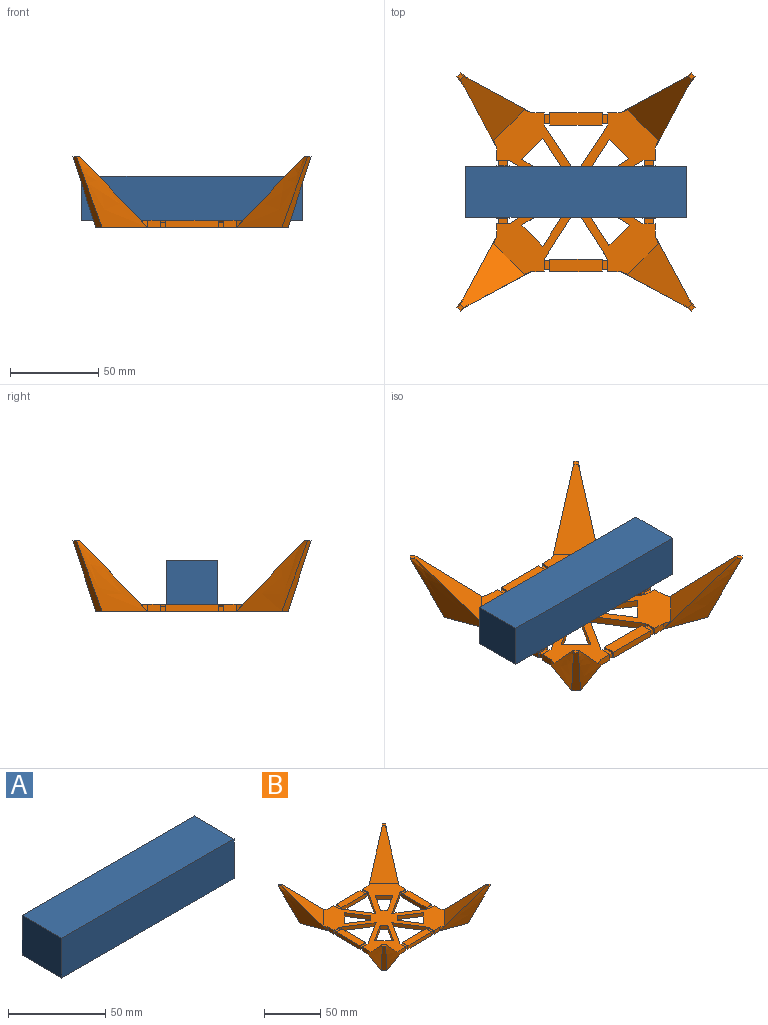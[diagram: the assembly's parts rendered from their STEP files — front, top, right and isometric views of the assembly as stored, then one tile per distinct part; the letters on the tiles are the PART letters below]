
ASSEMBLY  parts=2 mates=1
PART A: 11 faces, bbox 125.1x29x25 mm
  f0: plane 28.98x25mm, normal (1,0,0), area 199.9mm2, adj f1,f3,f4,f5,f6,f8,f9,f10
  f1: plane 125.11x25mm, normal (0,1,0), area 3127.8mm2, adj f0,f2,f4,f5
  f2: plane 28.98x25mm, normal (-1,0,0), area 724.4mm2, adj f1,f3,f4,f5
  f3: plane 125.11x25mm, normal (0,-1,0), area 3127.8mm2, adj f0,f2,f4,f5
  f4: plane 125.11x28.98mm, normal (0,0,1), area 3625.5mm2, adj f0,f1,f2,f3
  f5: plane 125.11x28.98mm, normal (0,0,-1), area 3625.5mm2, adj f0,f1,f2,f3
  f6: plane 123.11x21mm, normal (0,-1,0), area 2585.4mm2, adj f0,f7,f9,f10
  f7: plane 24.98x21mm, normal (1,0,0), area 524.5mm2, adj f6,f8,f9,f10
  f8: plane 123.11x21mm, normal (0,1,0), area 2585.4mm2, adj f0,f7,f9,f10
  f9: plane 123.11x24.98mm, normal (0,0,-1), area 3075mm2, adj f0,f6,f7,f8
  f10: plane 123.11x24.98mm, normal (0,0,1), area 3075mm2, adj f0,f6,f7,f8
PART B: 169 faces, bbox 135x135x40 mm
  f0: plane 108.95x108.91mm, normal (0,0,-1), area 4796.5mm2, adj f1,f2,f3,f4,f5,f6,f7,f8
  f1: plane 3x3mm, normal (0,-1,0), area 9mm2, adj f0,f19,f20,f111
  f2: plane 3x2.99mm, normal (0,1,0), area 9mm2, adj f0,f40,f41,f107
  f3: plane 3x3mm, normal (-1,0,0), area 9mm2, adj f0,f50,f51,f109
  f4: plane 3x2.98mm, normal (-1,0,0), area 8.9mm2, adj f0,f53,f97,f110
  f5: plane 3x3mm, normal (0,1,0), area 9mm2, adj f0,f57,f58,f112
  f6: plane 3x2.99mm, normal (0.01,-1,0), area 9mm2, adj f0,f71,f72,f101
  f7: plane 4x3mm, normal (0,-1,0), area 9mm2, adj f0,f41,f74,f75,f98,f107
  f8: plane 3x3mm, normal (1,0,0), area 9mm2, adj f0,f50,f86,f109
  f9: plane 3x2.98mm, normal (1,0,0), area 8.9mm2, adj f0,f89,f97,f110
  f10: plane 3x3mm, normal (0,1,0), area 9mm2, adj f0,f20,f54,f111
  f11: plane 29.88x7.06mm, normal (0,0,1), area 210.8mm2, adj f31,f32,f33,f64,f65,f66,f104
  f12: plane 93.17x93.16mm, normal (0,0,1), area 3663.2mm2, adj f15,f16,f17,f18,f19,f24,f25,f26
  f13: plane 29.88x7.07mm, normal (0,0,1), area 211.3mm2, adj f51,f52,f53,f86,f89,f96,f108
  f14: plane 29.86x7.06mm, normal (0,0,1), area 210.5mm2, adj f20,f21,f22,f23,f58,f59
  f15: plane 7.08x4mm, normal (-1,0,0), area 28.3mm2, adj f0,f12,f16,f97
  f16: plane 4.36x4.03mm, normal (-0.94,0.34,0), area 9.2mm2, adj f12,f15,f120
  f17: plane 4.35x4.03mm, normal (0.34,-0.94,0), area 9.2mm2, adj f12,f18,f120
  f18: plane 7.08x4mm, normal (0,-1,0), area 28.3mm2, adj f0,f12,f17,f19
  f19: plane 4x1mm, normal (1,0,0), area 4mm2, adj f0,f1,f12,f18,f54
  f20: plane 7.04x4mm, normal (-1,0,0), area 12.9mm2, adj f0,f1,f10,f14,f21,f59,f111
  f21: plane 29.85x4mm, normal (0,-1,0), area 119.4mm2, adj f0,f14,f20,f22
  f22: plane 4x0.99mm, normal (1,0,0), area 3.9mm2, adj f0,f14,f21,f23
  f23: plane 4x3.02mm, normal (0,-1,0), area 9.1mm2, adj f0,f14,f22,f24,f58,f112
  f24: plane 6.07x4mm, normal (-1,0,0), area 9mm2, adj f0,f12,f23,f25,f57,f112
  f25: plane 7.07x4mm, normal (0,-1,0), area 28.3mm2, adj f0,f12,f24,f26
  f26: plane 4.36x4.03mm, normal (-0.34,-0.94,0), area 9.2mm2, adj f12,f25,f116
  f27: plane 4.35x4.03mm, normal (0.94,0.34,0), area 9.2mm2, adj f12,f28,f116
  f28: plane 7.08x4mm, normal (1,0,0), area 28.3mm2, adj f0,f12,f27,f29
  f29: plane 4x1mm, normal (0,1,0), area 4mm2, adj f0,f12,f28,f30,f102
  f30: plane 3x2.98mm, normal (1,0,0), area 8.9mm2, adj f0,f29,f31,f103
  f31: plane 6.08x4.01mm, normal (0,-1,0), area 9mm2, adj f0,f11,f30,f32,f66,f103
  f32: plane 29.87x4mm, normal (1,0,0), area 119.5mm2, adj f0,f11,f31,f33
  f33: plane 4.01x1mm, normal (0,1,0), area 4mm2, adj f0,f11,f32,f34,f104
  f34: plane 3x3mm, normal (1,0,0), area 9mm2, adj f0,f33,f35,f105
  f35: plane 6.1x4mm, normal (0,-1,0), area 9.1mm2, adj f0,f12,f34,f36,f62,f105
  f36: plane 7.07x4mm, normal (1,0,0), area 28.3mm2, adj f0,f12,f35,f37
  f37: plane 4.36x4.03mm, normal (0.94,-0.34,0), area 9.2mm2, adj f12,f36,f126
  f38: plane 4.35x4.03mm, normal (-0.34,0.94,0), area 9.2mm2, adj f12,f39,f126
  f39: plane 7.08x4mm, normal (0,1,0), area 28.3mm2, adj f0,f12,f38,f40
  f40: plane 4.01x1.01mm, normal (-1,0,0), area 4mm2, adj f0,f2,f12,f39,f106
  f41: plane 6.09x4mm, normal (1,0,0), area 9.1mm2, adj f0,f2,f7,f42,f98,f107
  f42: plane 29.87x4mm, normal (0,1,0), area 119.5mm2, adj f0,f41,f43,f98
  f43: plane 6.08x4mm, normal (-1,0,0), area 9mm2, adj f0,f42,f44,f98,f100,f101
  f44: plane 3x2.99mm, normal (0,1,0), area 9mm2, adj f0,f43,f45,f101
  f45: plane 4.01x0.96mm, normal (1,0,0), area 3.8mm2, adj f0,f12,f44,f46,f99
  f46: plane 7.08x4mm, normal (0,1,0), area 28.3mm2, adj f0,f12,f45,f47
  f47: plane 4.35x4.03mm, normal (0.34,0.94,0), area 9.2mm2, adj f12,f46,f131
  f48: plane 4.35x4.03mm, normal (-0.94,-0.34,0), area 9.2mm2, adj f12,f49,f131
  f49: plane 7.09x4mm, normal (-1,0,0), area 28.4mm2, adj f0,f12,f48,f50
  f50: plane 7.09x4mm, normal (0,-1,0), area 13.1mm2, adj f0,f3,f8,f12,f49,f87,f109
  f51: plane 4x1mm, normal (0,1,0), area 4mm2, adj f0,f3,f13,f52,f108
  f52: plane 29.87x4mm, normal (-1,0,0), area 119.5mm2, adj f0,f13,f51,f53
  f53: plane 6.09x4.01mm, normal (0,-1,0), area 9.1mm2, adj f0,f4,f13,f52,f89,f110
  f54: plane 6.07x4mm, normal (1,0,0), area 9mm2, adj f0,f10,f12,f19,f55,f111
  f55: plane 27.99x17.94mm, normal (0.84,-0.54,0), area 133mm2, adj f0,f12,f54,f56
  f56: plane 27.98x17.92mm, normal (-0.84,-0.54,0), area 132.9mm2, adj f0,f12,f55,f57
  f57: plane 4x1.01mm, normal (-1,0,0), area 4mm2, adj f0,f5,f12,f24,f56
  f58: plane 6.07x4mm, normal (1,0,0), area 9.1mm2, adj f0,f5,f14,f23,f59,f112
  f59: plane 29.86x4mm, normal (0,1,0), area 119.4mm2, adj f0,f14,f20,f58
  f60: plane 27.99x17.91mm, normal (0.54,0.84,0), area 132.9mm2, adj f0,f12,f61,f90
  f61: plane 27.99x17.94mm, normal (0.54,-0.84,0), area 133mm2, adj f0,f12,f60,f62
  f62: plane 4x0.96mm, normal (0,-1,0), area 3.9mm2, adj f0,f12,f35,f61,f63
  f63: plane 3x3mm, normal (-1,0,0), area 9mm2, adj f0,f62,f64,f105
  f64: plane 4x0.96mm, normal (0,1,0), area 3.9mm2, adj f0,f11,f63,f65,f104
  f65: plane 29.87x4mm, normal (-1,0,0), area 119.5mm2, adj f0,f11,f64,f66
  f66: plane 4.01x1mm, normal (0,-1,0), area 3.9mm2, adj f0,f11,f31,f65,f67
  f67: plane 3x2.98mm, normal (-1,0,0), area 8.9mm2, adj f0,f66,f90,f103
  f68: plane 19.97x12.79mm, normal (0.84,0.54,0), area 94.9mm2, adj f0,f12,f69,f91
  f69: plane 4.78x4.7mm, normal (0.71,-0.7,0), area 26.8mm2, adj f0,f12,f68,f70
  f70: plane 19.84x12.97mm, normal (-0.55,-0.84,0), area 94.8mm2, adj f0,f12,f69,f91
  f71: plane 4x0.99mm, normal (1,0,0), area 3.9mm2, adj f0,f6,f12,f92,f99
  f72: plane 4x1.01mm, normal (-1,0,0), area 4mm2, adj f0,f6,f73,f98,f100,f101
  f73: plane 29.86x4mm, normal (0,-1,0), area 119.4mm2, adj f0,f72,f74,f98
  f74: plane 4x0.99mm, normal (1,0,0), area 3.9mm2, adj f0,f7,f73,f98
  f75: plane 4x0.99mm, normal (-1,0,0), area 3.9mm2, adj f0,f7,f12,f76,f106
  f76: plane 27.72x17.92mm, normal (-0.84,0.54,0), area 132mm2, adj f0,f12,f75,f92
  f77: plane 11.94x11.84mm, normal (0.71,-0.7,0), area 67.3mm2, adj f0,f12,f78,f93
  f78: plane 20.16x12.91mm, normal (-0.84,-0.54,0), area 95.8mm2, adj f0,f12,f77,f79
  f79: plane 4.65x4.64mm, normal (-0.71,0.71,0), area 26.3mm2, adj f0,f12,f78,f93
  f80: plane 19.32x12.5mm, normal (-0.54,0.84,0), area 92mm2, adj f0,f12,f81,f94
  f81: plane 4.23x4.22mm, normal (0.71,0.71,0), area 23.9mm2, adj f0,f12,f80,f82
  f82: plane 19.4x12.41mm, normal (0.84,-0.54,0), area 92.1mm2, adj f0,f12,f81,f94
  f83: plane 11.88x11.86mm, normal (0.71,0.71,0), area 67.2mm2, adj f0,f12,f84,f95
  f84: plane 20.08x12.86mm, normal (0.54,-0.84,0), area 95.4mm2, adj f0,f12,f83,f85
  f85: plane 4.67x4.66mm, normal (-0.71,-0.71,0), area 26.4mm2, adj f0,f12,f84,f95
  f86: plane 4x1mm, normal (0,1,0), area 4mm2, adj f0,f8,f13,f96,f108
  f87: plane 27.97x17.94mm, normal (-0.54,-0.84,0), area 132.9mm2, adj f0,f12,f50,f88
  f88: plane 27.97x17.91mm, normal (-0.54,0.84,0), area 132.9mm2, adj f0,f12,f87,f97
  f89: plane 4.01x1mm, normal (0,-1,0), area 4mm2, adj f0,f9,f13,f53,f96
  f90: plane 4x0.99mm, normal (0,1,0), area 3.9mm2, adj f0,f12,f60,f67,f102
  f91: plane 11.78x11.76mm, normal (-0.71,0.71,0), area 66.6mm2, adj f0,f12,f68,f70
  f92: plane 27.73x17.94mm, normal (0.84,0.54,0), area 132.1mm2, adj f0,f12,f71,f76
  f93: plane 20.11x12.86mm, normal (0.54,0.84,0), area 95.5mm2, adj f0,f12,f77,f79
  f94: plane 11.14x11.12mm, normal (-0.71,-0.71,0), area 63mm2, adj f0,f12,f80,f82
  f95: plane 20.06x12.86mm, normal (-0.84,0.54,0), area 95.3mm2, adj f0,f12,f83,f85
  f96: plane 29.87x4mm, normal (1,0,0), area 119.5mm2, adj f0,f13,f86,f89
  f97: plane 7.09x4mm, normal (0,1,0), area 13.1mm2, adj f0,f4,f9,f12,f15,f88,f110
  f98: plane 29.87x7.08mm, normal (0,0,1), area 211.3mm2, adj f7,f41,f42,f43,f72,f73,f74,f100
  f99: plane 5.11x1.01mm, normal (1,0,0), area 5.1mm2, adj f12,f45,f71,f101
  f100: plane 1x0mm, normal (0,1,0), area 0mm2, adj f43,f72,f98,f101
  f101: plane 5.1x3mm, normal (0,0,1), area 15.3mm2, adj f6,f43,f44,f72,f99,f100
  f102: plane 5.08x1mm, normal (0,1,0), area 5.1mm2, adj f12,f29,f90,f103
  f103: plane 5.08x2.98mm, normal (0,0,1), area 15.1mm2, adj f30,f31,f67,f102
  f104: plane 5.11x1.01mm, normal (0,1,0), area 5.1mm2, adj f11,f33,f64,f105
  f105: plane 5.1x3mm, normal (0,0,1), area 15.3mm2, adj f34,f35,f63,f104
  f106: plane 5.12x1.01mm, normal (-1,0,0), area 5.1mm2, adj f12,f40,f75,f107
  f107: plane 5.11x2.99mm, normal (0,0,1), area 15.3mm2, adj f2,f7,f41,f106
  f108: plane 5.08x1mm, normal (0,1,0), area 5.1mm2, adj f13,f51,f86,f109
  f109: plane 5.07x3mm, normal (0,0,1), area 15.2mm2, adj f3,f8,f50,f108
  f110: plane 5.09x2.98mm, normal (0,0,1), area 15.2mm2, adj f4,f9,f53,f97
  f111: plane 5.09x3mm, normal (0,0,1), area 15.3mm2, adj f1,f10,f20,f54
  f112: plane 5.07x3mm, normal (0,0,1), area 15.2mm2, adj f5,f23,f24,f58
  f113: plane 4x4mm, normal (0,0,1), area 8mm2, adj f114,f115,f116,f117
  f114: bspline ~40x16.66mm, area 175.4mm2, adj f0,f113,f115,f117
  f115: bspline ~40.51x40mm, area 610.2mm2, adj f0,f113,f114,f116
  f116: bspline ~40.51x40.51mm, area 747.1mm2, adj f12,f26,f27,f113,f115,f117
  f117: bspline ~40.51x40mm, area 609.5mm2, adj f0,f113,f114,f116
  f118: plane 4x4mm, normal (0,0,1), area 8mm2, adj f119,f120,f121,f122
  f119: bspline ~40.51x40mm, area 610.9mm2, adj f0,f118,f120,f122
  f120: bspline ~40.51x40.49mm, area 747.1mm2, adj f12,f16,f17,f118,f119,f121
  f121: bspline ~40.49x40mm, area 610.2mm2, adj f0,f118,f120,f122
  f122: bspline ~40x16.6mm, area 174.8mm2, adj f0,f118,f119,f121
  f123: plane 4x4mm, normal (0,0,1), area 8mm2, adj f124,f125,f126,f127
  f124: bspline ~40x16.63mm, area 175.2mm2, adj f0,f123,f125,f127
  f125: bspline ~40.49x40mm, area 610.4mm2, adj f0,f123,f124,f126
  f126: bspline ~40.51x40.49mm, area 747.1mm2, adj f12,f37,f38,f123,f125,f127
  f127: bspline ~40.51x40mm, area 610mm2, adj f0,f123,f124,f126
  f128: plane 4x4mm, normal (0,0,1), area 8mm2, adj f129,f130,f131,f132
  f129: bspline ~40x16.62mm, area 174.8mm2, adj f0,f128,f130,f132
  f130: bspline ~40.49x40mm, area 609.7mm2, adj f0,f128,f129,f131
  f131: bspline ~40.49x40.47mm, area 746.2mm2, adj f12,f47,f48,f128,f130,f132
  f132: bspline ~40.47x40mm, area 609.5mm2, adj f0,f128,f129,f131
  f133: plane 17.94x17.94mm, normal (-0.71,0.71,0), area 12.7mm2, adj f134,f136,f137,f162
  f134: plane 3.54x3.54mm, normal (-0.71,-0.71,0), area 2.5mm2, adj f133,f135,f137,f164
  f135: plane 17.94x17.94mm, normal (0.71,-0.71,0), area 12.7mm2, adj f134,f136,f137,f163
  f136: plane 3.54x3.54mm, normal (0.71,0.71,0), area 2.5mm2, adj f133,f135,f137,f161
  f137: plane 21.48x21.48mm, normal (0,0,-1), area 126.9mm2, adj f133,f134,f135,f136
  f138: plane 17.94x17.94mm, normal (0.71,-0.71,0), area 12.7mm2, adj f139,f141,f142,f154
  f139: plane 3.54x3.54mm, normal (0.71,0.71,0), area 2.5mm2, adj f138,f140,f142,f156
  f140: plane 17.94x17.94mm, normal (-0.71,0.71,0), area 12.7mm2, adj f139,f141,f142,f155
  f141: plane 3.54x3.54mm, normal (-0.71,-0.71,0), area 2.5mm2, adj f138,f140,f142,f153
  f142: plane 21.48x21.48mm, normal (0,0,-1), area 126.9mm2, adj f138,f139,f140,f141
  f143: plane 17.94x17.94mm, normal (-0.71,-0.71,0), area 12.7mm2, adj f144,f146,f147,f166
  f144: plane 3.54x3.54mm, normal (0.71,-0.71,0), area 2.5mm2, adj f143,f145,f147,f168
  f145: plane 17.94x17.94mm, normal (0.71,0.71,0), area 12.7mm2, adj f144,f146,f147,f167
  f146: plane 3.54x3.54mm, normal (-0.71,0.71,0), area 2.5mm2, adj f143,f145,f147,f165
  f147: plane 21.48x21.48mm, normal (0,0,-1), area 126.9mm2, adj f143,f144,f145,f146
  f148: plane 17.94x17.94mm, normal (0.71,0.71,0), area 12.7mm2, adj f149,f151,f152,f158
  f149: plane 3.54x3.54mm, normal (-0.71,0.71,0), area 2.5mm2, adj f148,f150,f152,f157
  f150: plane 17.94x17.94mm, normal (-0.71,-0.71,0), area 12.7mm2, adj f149,f151,f152,f159
  f151: plane 3.54x3.54mm, normal (0.71,-0.71,0), area 2.5mm2, adj f148,f150,f152,f160
  f152: plane 21.48x21.48mm, normal (0,0,-1), area 126.9mm2, adj f148,f149,f150,f151
  f153: plane 6.36x6.36mm, normal (-0.5,-0.5,-0.71), area 19.8mm2, adj f0,f141,f154,f155
  f154: plane 20.77x20.77mm, normal (0.5,-0.5,-0.71), area 77.4mm2, adj f0,f138,f153,f156
  f155: plane 20.77x20.77mm, normal (-0.5,0.5,-0.71), area 77.4mm2, adj f0,f140,f153,f156
  f156: plane 6.36x6.36mm, normal (0.5,0.5,-0.71), area 19.8mm2, adj f0,f139,f154,f155
  f157: plane 6.36x6.36mm, normal (-0.5,0.5,-0.71), area 19.8mm2, adj f0,f149,f158,f159
  f158: plane 20.77x20.77mm, normal (0.5,0.5,-0.71), area 77.4mm2, adj f0,f148,f157,f160
  f159: plane 20.77x20.77mm, normal (-0.5,-0.5,-0.71), area 77.4mm2, adj f0,f150,f157,f160
  f160: plane 6.36x6.36mm, normal (0.5,-0.5,-0.71), area 19.8mm2, adj f0,f151,f158,f159
  f161: plane 6.36x6.36mm, normal (0.5,0.5,-0.71), area 19.8mm2, adj f0,f136,f162,f163
  f162: plane 20.77x20.77mm, normal (-0.5,0.5,-0.71), area 77.4mm2, adj f0,f133,f161,f164
  f163: plane 20.77x20.77mm, normal (0.5,-0.5,-0.71), area 77.4mm2, adj f0,f135,f161,f164
  f164: plane 6.36x6.36mm, normal (-0.5,-0.5,-0.71), area 19.8mm2, adj f0,f134,f162,f163
  f165: plane 6.36x6.36mm, normal (-0.5,0.5,-0.71), area 19.8mm2, adj f0,f146,f166,f167
  f166: plane 20.77x20.77mm, normal (-0.5,-0.5,-0.71), area 77.4mm2, adj f0,f143,f165,f168
  f167: plane 20.77x20.77mm, normal (0.5,0.5,-0.71), area 77.4mm2, adj f0,f145,f165,f168
  f168: plane 6.36x6.36mm, normal (0.5,-0.5,-0.71), area 19.8mm2, adj f0,f144,f166,f167
PLACE A t=(0.14,0.16,4)mm
PLACE B at identity
MATE fastened A.f5 <-> B.f12  axis (0,0,-1) through (0.14,0.16,4)mm
